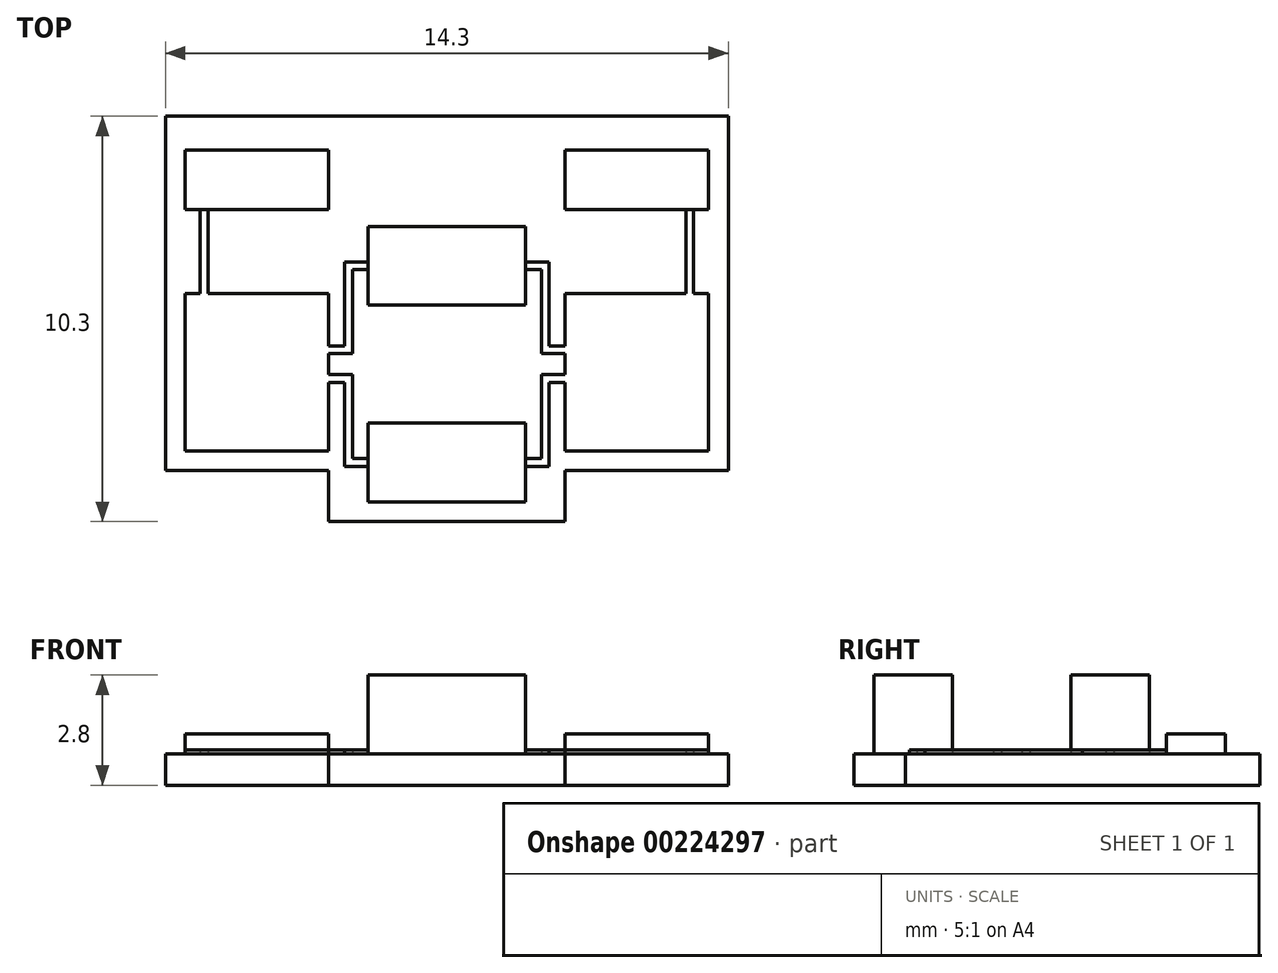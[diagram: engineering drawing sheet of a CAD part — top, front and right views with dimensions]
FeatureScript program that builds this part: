
annotation { "Feature Type Name" : "Feature", "Feature Type Description" : "" }
export const myFeature = defineFeature(function(context is Context, id is Id, definition is map)
    precondition{}
    {
        {
            var Q0;
            Q0=qCreatedBy(makeId("Top.planeOp"),FACE);
            var sketch = newSketch(context, id + "F0", { "sketchPlane" : qUnion([Q0])});
            skLineSegment(sketch, "E0.bottom", {"start": v(-7.15, 4.5) * mm, "end": v(7.15, 4.5) * mm});
            skLineSegment(sketch, "E0.top", {"start": v(-7.15, -4.5) * mm, "end": v(-3, -4.5) * mm});
            skLineSegment(sketch, "E0.left", {"start": v(-7.15, 4.5) * mm, "end": v(-7.15, -4.5) * mm});
            skLineSegment(sketch, "E0.right", {"start": v(7.15, 4.5) * mm, "end": v(7.15, -4.5) * mm});
            skPoint(sketch, "E0.middle", {"position": v(0, 0) * mm});
            skLineSegment(sketch, "E1.bottom", {"start": v(3, -5.8) * mm, "end": v(-3, -5.8) * mm});
            skLineSegment(sketch, "E1.left", {"start": v(3, -5.8) * mm, "end": v(3, -4.5) * mm});
            skLineSegment(sketch, "E1.right", {"start": v(-3, -5.8) * mm, "end": v(-3, -4.5) * mm});
            skPoint(sketch, "E1.middle", {"position": v(0, -4.5) * mm});
            skPoint(sketch, "E2.orphan", {"position": v(3, -3.2) * mm});
            skPoint(sketch, "E3.orphan", {"position": v(-3, -3.2) * mm});
            skLineSegment(sketch, "E4.trimOffspring", {"start": v(3, -4.5) * mm, "end": v(7.15, -4.5) * mm});
            skLineSegment(sketch, "E5.bottom", {"start": v(-6.65, -4) * mm, "end": v(-3, -4) * mm});
            skLineSegment(sketch, "E5.top", {"start": v(-6.65, 0) * mm, "end": v(-3, 0) * mm});
            skLineSegment(sketch, "E5.left", {"start": v(-6.65, -4) * mm, "end": v(-6.65, 0) * mm});
            skLineSegment(sketch, "E5.right", {"start": v(-3, -4) * mm, "end": v(-3, 0) * mm});
            skLineSegment(sketch, "E6", {"start": v(0, -4.5) * mm, "end": v(0, 0) * mm, "construction": true});
            skLineSegment(sketch, "E7.MirrorCS", {"start": v(6.65, 0) * mm, "end": v(3, 0) * mm});
            skLineSegment(sketch, "E8.MirrorCS", {"start": v(6.65, -4) * mm, "end": v(6.65, 0) * mm});
            skLineSegment(sketch, "E9.MirrorCS", {"start": v(6.65, -4) * mm, "end": v(3, -4) * mm});
            skLineSegment(sketch, "E10.MirrorCS", {"start": v(3, -4) * mm, "end": v(3, 0) * mm});
            skLineSegment(sketch, "E11", {"start": v(0, -4.5) * mm, "end": v(0, -5.8) * mm, "construction": true});
            skLineSegment(sketch, "E12.bottom", {"start": v(-2, -5.3) * mm, "end": v(2, -5.3) * mm});
            skLineSegment(sketch, "E12.top", {"start": v(-2, -3.3) * mm, "end": v(2, -3.3) * mm});
            skLineSegment(sketch, "E12.left", {"start": v(-2, -5.3) * mm, "end": v(-2, -3.3) * mm});
            skLineSegment(sketch, "E12.right", {"start": v(2, -5.3) * mm, "end": v(2, -3.3) * mm});
            skPoint(sketch, "E13", {"position": v(0, -3.3) * mm});
            skLineSegment(sketch, "E14", {"start": v(-0.9, -1.8) * mm, "end": v(0.9, -1.8) * mm, "construction": true});
            skPoint(sketch, "E15", {"position": v(0, -1.8) * mm});
            skLineSegment(sketch, "E16.MirrorCS", {"start": v(-2, -0.3) * mm, "end": v(2, -0.3) * mm});
            skLineSegment(sketch, "E17.MirrorCS", {"start": v(-2, 1.7) * mm, "end": v(-2, -0.3) * mm});
            skLineSegment(sketch, "E18.MirrorCS", {"start": v(-2, 1.7) * mm, "end": v(2, 1.7) * mm});
            skLineSegment(sketch, "E19.MirrorCS", {"start": v(2, 1.7) * mm, "end": v(2, -0.3) * mm});
            skLineSegment(sketch, "E20.bottom", {"start": v(-6.65, 3.63) * mm, "end": v(-3, 3.63) * mm});
            skLineSegment(sketch, "E20.top", {"start": v(-6.65, 2.13) * mm, "end": v(-3, 2.13) * mm});
            skLineSegment(sketch, "E20.left", {"start": v(-6.65, 3.63) * mm, "end": v(-6.65, 2.13) * mm});
            skLineSegment(sketch, "E20.right", {"start": v(-3, 3.63) * mm, "end": v(-3, 2.13) * mm});
            skLineSegment(sketch, "E21", {"start": v(0, 0) * mm, "end": v(0, 4.5) * mm, "construction": true});
            skLineSegment(sketch, "E22.MirrorCS", {"start": v(6.65, 3.63) * mm, "end": v(3, 3.63) * mm});
            skLineSegment(sketch, "E23.MirrorCS", {"start": v(3, 3.63) * mm, "end": v(3, 2.13) * mm});
            skLineSegment(sketch, "E24.MirrorCS", {"start": v(6.65, 2.13) * mm, "end": v(3, 2.13) * mm});
            skLineSegment(sketch, "E25.MirrorCS", {"start": v(6.65, 3.63) * mm, "end": v(6.65, 2.13) * mm});
            skPoint(sketch, "E26", {"position": v(-2, 0.7) * mm});
            skPoint(sketch, "E27", {"position": v(2, 0.7) * mm});
            skPoint(sketch, "E28", {"position": v(2, -4.3) * mm});
            skPoint(sketch, "E29", {"position": v(-2, -4.3) * mm});
            skLineSegment(sketch, "E30", {"start": v(-6.27, 2.13) * mm, "end": v(-6.27, 0) * mm});
            skLineSegment(sketch, "E31", {"start": v(-6.27, 0) * mm, "end": v(-6.07, 0) * mm});
            skLineSegment(sketch, "E32", {"start": v(-6.07, 0) * mm, "end": v(-6.07, 2.13) * mm});
            skLineSegment(sketch, "E33", {"start": v(-2, 0.8) * mm, "end": v(-2.6, 0.8) * mm});
            skLineSegment(sketch, "E34", {"start": v(-2.6, 0.8) * mm, "end": v(-2.6, -1.33) * mm});
            skLineSegment(sketch, "E35", {"start": v(-2.6, -1.33) * mm, "end": v(-3, -1.33) * mm});
            skLineSegment(sketch, "E36.0", {"start": v(-2.4, -1.53) * mm, "end": v(-3, -1.53) * mm});
            skLineSegment(sketch, "E36.1", {"start": v(-2.4, 0.6) * mm, "end": v(-2.4, -1.53) * mm});
            skLineSegment(sketch, "E36.2", {"start": v(-2, 0.6) * mm, "end": v(-2.4, 0.6) * mm});
            skLineSegment(sketch, "E37.MirrorCS", {"start": v(-2.4, -4.2) * mm, "end": v(-2.4, -2.07) * mm});
            skLineSegment(sketch, "E38.MirrorCS", {"start": v(-2.6, -4.4) * mm, "end": v(-2.6, -2.27) * mm});
            skLineSegment(sketch, "E39.MirrorCS", {"start": v(-2, -4.4) * mm, "end": v(-2.6, -4.4) * mm});
            skLineSegment(sketch, "E40.MirrorCS", {"start": v(-2, -4.2) * mm, "end": v(-2.4, -4.2) * mm});
            skLineSegment(sketch, "E41.MirrorCS", {"start": v(-2.6, -2.27) * mm, "end": v(-3, -2.27) * mm});
            skLineSegment(sketch, "E42.MirrorCS", {"start": v(-2.4, -2.07) * mm, "end": v(-3, -2.07) * mm});
            skLineSegment(sketch, "E43.MirrorCS", {"start": v(6.07, 0) * mm, "end": v(6.07, 2.13) * mm});
            skLineSegment(sketch, "E44.MirrorCS", {"start": v(6.27, 2.13) * mm, "end": v(6.27, 0) * mm});
            skLineSegment(sketch, "E45.MirrorCS", {"start": v(2.4, 0.6) * mm, "end": v(2.4, -1.53) * mm});
            skLineSegment(sketch, "E46.MirrorCS", {"start": v(2, 0.6) * mm, "end": v(2.4, 0.6) * mm});
            skLineSegment(sketch, "E47.MirrorCS", {"start": v(2, 0.8) * mm, "end": v(2.6, 0.8) * mm});
            skLineSegment(sketch, "E48.MirrorCS", {"start": v(2.6, 0.8) * mm, "end": v(2.6, -1.33) * mm});
            skLineSegment(sketch, "E49.MirrorCS", {"start": v(2.6, -1.33) * mm, "end": v(3, -1.33) * mm});
            skLineSegment(sketch, "E50.MirrorCS", {"start": v(2.4, -1.53) * mm, "end": v(3, -1.53) * mm});
            skLineSegment(sketch, "E51.MirrorCS", {"start": v(2.4, -2.07) * mm, "end": v(3, -2.07) * mm});
            skLineSegment(sketch, "E52.MirrorCS", {"start": v(2.6, -2.27) * mm, "end": v(3, -2.27) * mm});
            skLineSegment(sketch, "E53.MirrorCS", {"start": v(2.6, -4.4) * mm, "end": v(2.6, -2.27) * mm});
            skLineSegment(sketch, "E54.MirrorCS", {"start": v(2.4, -4.2) * mm, "end": v(2.4, -2.07) * mm});
            skLineSegment(sketch, "E55.MirrorCS", {"start": v(2, -4.2) * mm, "end": v(2.4, -4.2) * mm});
            skLineSegment(sketch, "E56.MirrorCS", {"start": v(2, -4.4) * mm, "end": v(2.6, -4.4) * mm});
            skSolve(sketch);
        }
        {
            var Q0;
            {var subQ5=sQuery(id+"F0.wireOp",EDGE,"E5.bottom");Q0=makeQuery(id+"F0.imprint","IMPRINT",FACE,{"disambiguationData":[TD([[makeQuery(id+"F0.imprint","IMPRINT",EDGE,{"derivedFrom":subQ5}),1.0]])]});}
            var Q1;
            {var subQ0=sQuery(id+"F0.wireOp",EDGE,"E30");Q1=makeQuery(id+"F0.imprint","IMPRINT",FACE,{"disambiguationData":[TD([[makeQuery(id+"F0.imprint","IMPRINT",EDGE,{"derivedFrom":subQ0}),1.0]])]});}
            var Q2;
            {var subQ0=sQuery(id+"F0.wireOp",EDGE,"E33");Q2=makeQuery(id+"F0.imprint","IMPRINT",FACE,{"disambiguationData":[TD([[makeQuery(id+"F0.imprint","IMPRINT",EDGE,{"derivedFrom":subQ0}),1.0]])]});}
            var Q3;
            Q3=makeQuery(id+"F0.imprint","IMPRINT",FACE,{"disambiguationData":[TD([[makeQuery(id+"F0.imprint","IMPRINT",EDGE,{"derivedFrom":sQuery(id+"F0.wireOp",EDGE,"E37.MirrorCS")}),1.0]])]});
            var Q4;
            {var subQ0=sQuery(id+"F0.wireOp",EDGE,"E8.MirrorCS");Q4=makeQuery(id+"F0.imprint","IMPRINT",FACE,{"disambiguationData":[TD([[makeQuery(id+"F0.imprint","IMPRINT",EDGE,{"derivedFrom":subQ0}),1.0]])]});}
            var Q5;
            {var subQ0=sQuery(id+"F0.wireOp",EDGE,"E43.MirrorCS");Q5=makeQuery(id+"F0.imprint","IMPRINT",FACE,{"disambiguationData":[TD([[makeQuery(id+"F0.imprint","IMPRINT",EDGE,{"derivedFrom":subQ0}),-1.0]])]});}
            var Q6;
            Q6=makeQuery(id+"F0.imprint","IMPRINT",FACE,{"disambiguationData":[TD([[makeQuery(id+"F0.imprint","IMPRINT",EDGE,{"derivedFrom":sQuery(id+"F0.wireOp",EDGE,"E45.MirrorCS")}),1.0]])]});
            var Q7;
            {var subQ1=sQuery(id+"F0.wireOp",EDGE,"E51.MirrorCS");Q7=makeQuery(id+"F0.imprint","IMPRINT",FACE,{"disambiguationData":[TD([[makeQuery(id+"F0.imprint","IMPRINT",EDGE,{"derivedFrom":subQ1}),-1.0]])]});}
            extrude(context, id + "F1", {"entities" : qUnion([Q0, Q1, Q2, Q3, Q4, Q5, Q6, Q7]), "depth" : 0.1 * mm});
        }
        {
            var Q0;
            Q0=makeQuery(id+"F0.imprint","IMPRINT",FACE,{"disambiguationData":[TD([[makeQuery(id+"F0.imprint","IMPRINT",EDGE,{"derivedFrom":sQuery(id+"F0.wireOp",EDGE,"E0.bottom")}),-1.0]])]});
            var Q1;
            {var subQ5=sQuery(id+"F0.wireOp",EDGE,"E12.top");Q1=makeQuery(id+"F0.imprint","IMPRINT",FACE,{"disambiguationData":[TD([[makeQuery(id+"F0.imprint","IMPRINT",EDGE,{"derivedFrom":subQ5}),1.0]])]});}
            var Q2;
            {var subQ5=sQuery(id+"F0.wireOp",EDGE,"E5.bottom");Q2=makeQuery(id+"F0.imprint","IMPRINT",FACE,{"disambiguationData":[TD([[makeQuery(id+"F0.imprint","IMPRINT",EDGE,{"derivedFrom":subQ5}),1.0]])]});}
            var Q3;
            Q3=makeQuery(id+"F0.imprint","IMPRINT",FACE,{"disambiguationData":[TD([[makeQuery(id+"F0.imprint","IMPRINT",EDGE,{"derivedFrom":sQuery(id+"F0.wireOp",EDGE,"E37.MirrorCS")}),1.0]])]});
            var Q4;
            {var subQ0=sQuery(id+"F0.wireOp",EDGE,"E33");Q4=makeQuery(id+"F0.imprint","IMPRINT",FACE,{"disambiguationData":[TD([[makeQuery(id+"F0.imprint","IMPRINT",EDGE,{"derivedFrom":subQ0}),1.0]])]});}
            var Q5;
            {var subQ3=sQuery(id+"F0.wireOp",EDGE,"E12.bottom");Q5=makeQuery(id+"F0.imprint","IMPRINT",FACE,{"disambiguationData":[TD([[makeQuery(id+"F0.imprint","IMPRINT",EDGE,{"derivedFrom":subQ3}),1.0]])]});}
            var Q6;
            {var subQ1=sQuery(id+"F0.wireOp",EDGE,"E16.MirrorCS");Q6=makeQuery(id+"F0.imprint","IMPRINT",FACE,{"disambiguationData":[TD([[makeQuery(id+"F0.imprint","IMPRINT",EDGE,{"derivedFrom":subQ1}),1.0]])]});}
            var Q7;
            Q7=makeQuery(id+"F0.imprint","IMPRINT",FACE,{"disambiguationData":[TD([[makeQuery(id+"F0.imprint","IMPRINT",EDGE,{"derivedFrom":sQuery(id+"F0.wireOp",EDGE,"E20.bottom")}),-1.0]])]});
            var Q8;
            {var subQ0=sQuery(id+"F0.wireOp",EDGE,"E30");Q8=makeQuery(id+"F0.imprint","IMPRINT",FACE,{"disambiguationData":[TD([[makeQuery(id+"F0.imprint","IMPRINT",EDGE,{"derivedFrom":subQ0}),1.0]])]});}
            var Q9;
            {var subQ0=sQuery(id+"F0.wireOp",EDGE,"E8.MirrorCS");Q9=makeQuery(id+"F0.imprint","IMPRINT",FACE,{"disambiguationData":[TD([[makeQuery(id+"F0.imprint","IMPRINT",EDGE,{"derivedFrom":subQ0}),1.0]])]});}
            var Q10;
            {var subQ1=sQuery(id+"F0.wireOp",EDGE,"E51.MirrorCS");Q10=makeQuery(id+"F0.imprint","IMPRINT",FACE,{"disambiguationData":[TD([[makeQuery(id+"F0.imprint","IMPRINT",EDGE,{"derivedFrom":subQ1}),-1.0]])]});}
            var Q11;
            Q11=makeQuery(id+"F0.imprint","IMPRINT",FACE,{"disambiguationData":[TD([[makeQuery(id+"F0.imprint","IMPRINT",EDGE,{"derivedFrom":sQuery(id+"F0.wireOp",EDGE,"E45.MirrorCS")}),1.0]])]});
            var Q12;
            Q12=makeQuery(id+"F0.imprint","IMPRINT",FACE,{"disambiguationData":[TD([[makeQuery(id+"F0.imprint","IMPRINT",EDGE,{"derivedFrom":sQuery(id+"F0.wireOp",EDGE,"E22.MirrorCS")}),1.0]])]});
            var Q13;
            {var subQ0=sQuery(id+"F0.wireOp",EDGE,"E43.MirrorCS");Q13=makeQuery(id+"F0.imprint","IMPRINT",FACE,{"disambiguationData":[TD([[makeQuery(id+"F0.imprint","IMPRINT",EDGE,{"derivedFrom":subQ0}),-1.0]])]});}
            extrude(context, id + "F2", {"entities" : qUnion([Q0, Q1, Q2, Q3, Q4, Q5, Q6, Q7, Q8, Q9, Q10, Q11, Q12, Q13]), "oppositeDirection" : true, "depth" : 0.8 * mm});
        }
        {
            var Q0;
            Q0=makeQuery(id+"F0.imprint","IMPRINT",FACE,{"disambiguationData":[TD([[makeQuery(id+"F0.imprint","IMPRINT",EDGE,{"derivedFrom":sQuery(id+"F0.wireOp",EDGE,"E20.bottom")}),-1.0]])]});
            var Q1;
            Q1=makeQuery(id+"F0.imprint","IMPRINT",FACE,{"disambiguationData":[TD([[makeQuery(id+"F0.imprint","IMPRINT",EDGE,{"derivedFrom":sQuery(id+"F0.wireOp",EDGE,"E22.MirrorCS")}),1.0]])]});
            extrude(context, id + "F3", {"entities" : qUnion([Q0, Q1]), "depth" : 0.5 * mm});
        }
        {
            var Q0;
            {var subQ1=sQuery(id+"F0.wireOp",EDGE,"E16.MirrorCS");Q0=makeQuery(id+"F0.imprint","IMPRINT",FACE,{"disambiguationData":[TD([[makeQuery(id+"F0.imprint","IMPRINT",EDGE,{"derivedFrom":subQ1}),1.0]])]});}
            var Q1;
            {var subQ3=sQuery(id+"F0.wireOp",EDGE,"E12.bottom");Q1=makeQuery(id+"F0.imprint","IMPRINT",FACE,{"disambiguationData":[TD([[makeQuery(id+"F0.imprint","IMPRINT",EDGE,{"derivedFrom":subQ3}),1.0]])]});}
            extrude(context, id + "F4", {"entities" : qUnion([Q0, Q1]), "depth" : 2 * mm});
        }
    });
